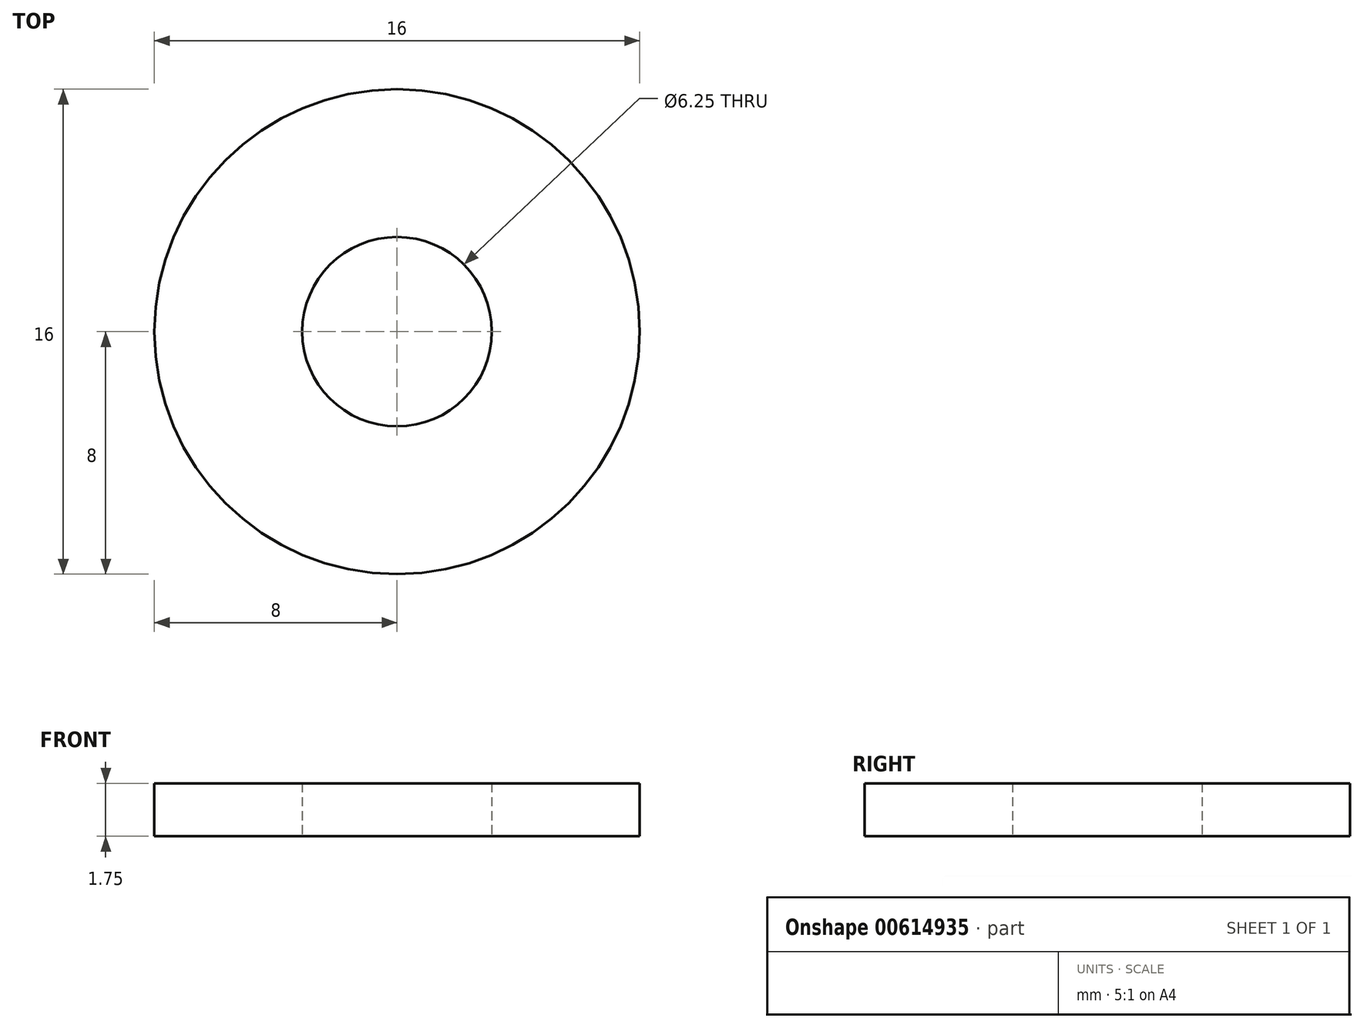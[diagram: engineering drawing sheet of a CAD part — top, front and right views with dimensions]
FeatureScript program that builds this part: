
annotation { "Feature Type Name" : "Feature", "Feature Type Description" : "" }
export const myFeature = defineFeature(function(context is Context, id is Id, definition is map)
    precondition{}
    {
        {
            var Q0;
            Q0=qCreatedBy(makeId("Top.planeOp"),FACE);
            var sketch = newSketch(context, id + "F0", { "sketchPlane" : qUnion([Q0])});
            skCircle(sketch, "E0", {"center": v(0, 0) * mm, "radius": 8 * mm});
            skCircle(sketch, "E1", {"center": v(0, 0) * mm, "radius": 3.12 * mm});
            skSolve(sketch);
        }
        {
            var Q0;
            Q0 = qSketchRegion(id + "F0", true);
            extrude(context, id + "F1", {"entities" : qUnion([Q0]), "depth" : 1.75 * mm, "offsetDistance" : 25 * mm});
        }
    });
